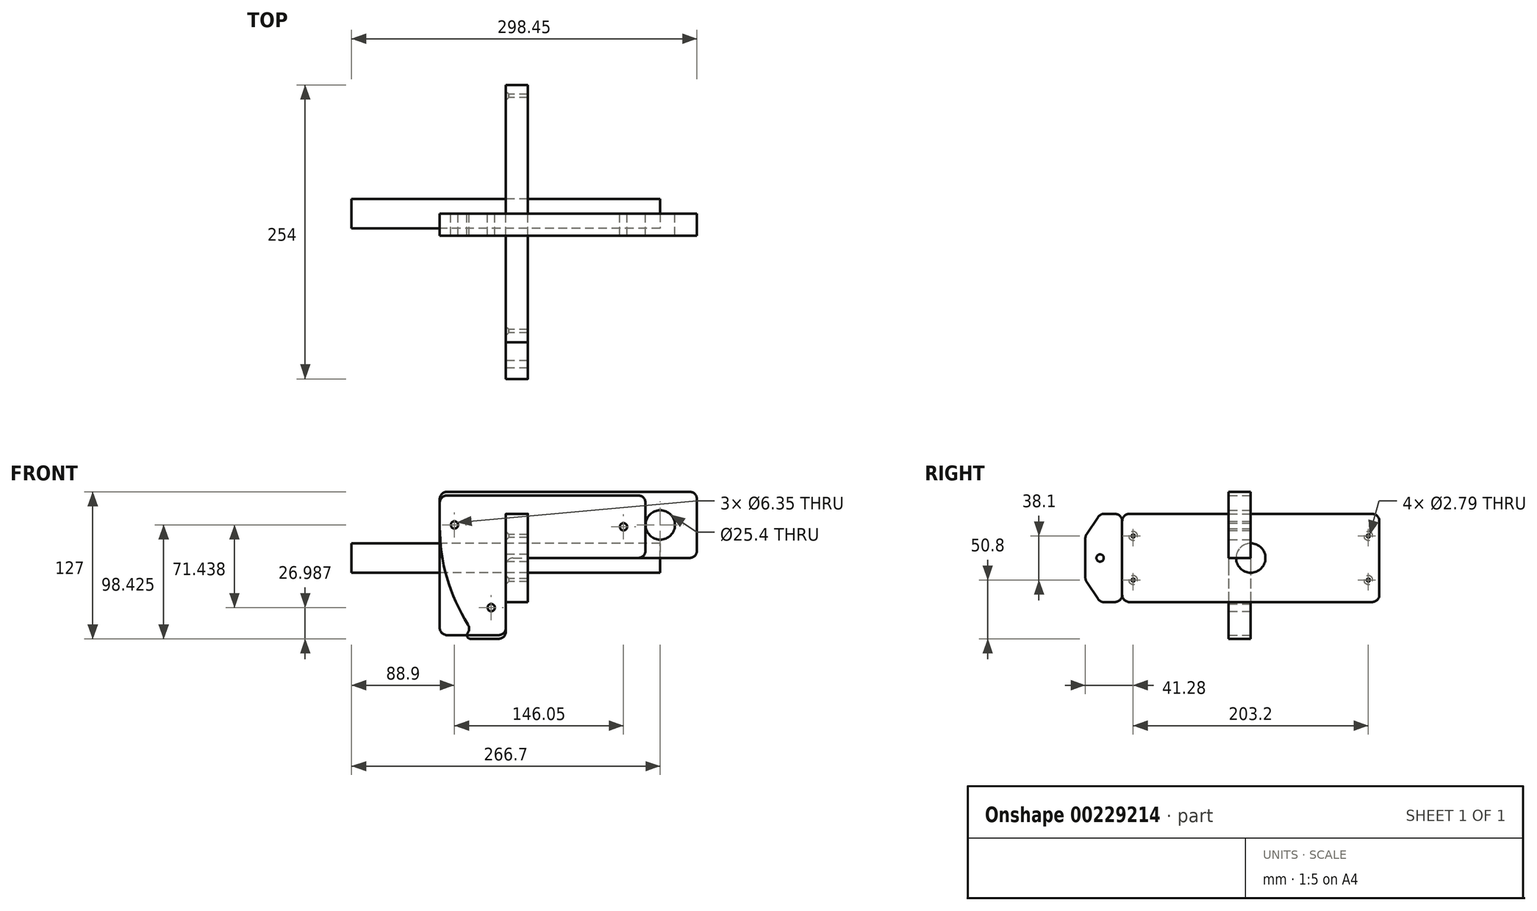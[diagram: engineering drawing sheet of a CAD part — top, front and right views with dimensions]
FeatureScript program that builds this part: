
annotation { "Feature Type Name" : "Feature", "Feature Type Description" : "" }
export const myFeature = defineFeature(function(context is Context, id is Id, definition is map)
    precondition{}
    {
        {
            var Q0;
            Q0=qCreatedBy(makeId("Front.planeOp"),FACE);
            var sketch = newSketch(context, id + "F0", { "sketchPlane" : qUnion([Q0])});
            skLineSegment(sketch, "E0", {"start": v(0, 0) * mm, "end": v(165.1, 0) * mm});
            skLineSegment(sketch, "E1", {"start": v(165.1, 0) * mm, "end": v(165.1, 57.15) * mm});
            skLineSegment(sketch, "E2", {"start": v(165.1, 57.15) * mm, "end": v(-57.15, 57.15) * mm});
            skLineSegment(sketch, "E3", {"start": v(-57.15, 57.15) * mm, "end": v(-57.15, -66.68) * mm});
            skLineSegment(sketch, "E4", {"start": v(-57.15, -66.68) * mm, "end": v(0, -66.68) * mm});
            skLineSegment(sketch, "E5", {"start": v(0, -66.68) * mm, "end": v(0, 0) * mm});
            skCircle(sketch, "E6", {"center": v(133.35, 28.58) * mm, "radius": 12.7 * mm});
            skPoint(sketch, "E6.centerSnap0", {"position": v(165.1, 28.58) * mm});
            skCircle(sketch, "E7", {"center": v(-44.45, 28.58) * mm, "radius": 3.17 * mm});
            skCircle(sketch, "E8", {"center": v(-12.7, -42.86) * mm, "radius": 3.18 * mm});
            skSolve(sketch);
        }
        {
            var Q0;
            Q0=makeQuery(id+"F0.imprint","IMPRINT",FACE,{"disambiguationData":[TD([[makeQuery(id+"F0.imprint","IMPRINT",EDGE,{"derivedFrom":sQuery(id+"F0.wireOp",EDGE,"E0")}),1.0]])]});
            extrude(context, id + "F1", {"entities" : qUnion([Q0]), "depth" : 19.05 * mm});
        }
        {
            var Q0;
            Q0=makeQuery(id+"F1.opExtrude","SWEPT_EDGE",EDGE,{"disambiguationData":[OSD([sQuery(id+"F0.wireOp",EDGE,"E0"),sQuery(id+"F0.wireOp",EDGE,"E5")])]});
            var Q1;
            Q1=makeQuery(id+"F1.opExtrude","SWEPT_EDGE",EDGE,{"disambiguationData":[OSD([sQuery(id+"F0.wireOp",EDGE,"E2"),sQuery(id+"F0.wireOp",EDGE,"E3")])]});
            var Q2;
            Q2=makeQuery(id+"F1.opExtrude","SWEPT_EDGE",EDGE,{"disambiguationData":[OSD([sQuery(id+"F0.wireOp",EDGE,"E1"),sQuery(id+"F0.wireOp",EDGE,"E2")])]});
            var Q3;
            Q3=makeQuery(id+"F1.opExtrude","SWEPT_EDGE",EDGE,{"disambiguationData":[OSD([sQuery(id+"F0.wireOp",EDGE,"E0"),sQuery(id+"F0.wireOp",EDGE,"E1")])]});
            var Q4;
            Q4=makeQuery(id+"F1.opExtrude","SWEPT_EDGE",EDGE,{"disambiguationData":[OSD([sQuery(id+"F0.wireOp",EDGE,"E3"),sQuery(id+"F0.wireOp",EDGE,"E4")])]});
            var Q5;
            Q5=makeQuery(id+"F1.opExtrude","SWEPT_EDGE",EDGE,{"disambiguationData":[OSD([sQuery(id+"F0.wireOp",EDGE,"E4"),sQuery(id+"F0.wireOp",EDGE,"E5")])]});
            fillet(context, id + "F2", {"entities" : qUnion([Q0, Q1, Q2, Q3, Q4, Q5]), "radius" : 6.35 * mm, "tangentPropagation" : true, "allowEdgeOverflow" : false});
        }
        {
            var Q0;
            Q0=qCreatedBy(makeId("Front.planeOp"),FACE);
            var sketch = newSketch(context, id + "F3", { "sketchPlane" : qUnion([Q0])});
            skLineSegment(sketch, "E9", {"start": v(0, 0) * mm, "end": v(120.65, 0) * mm});
            skLineSegment(sketch, "E10", {"start": v(120.65, 0) * mm, "end": v(120.65, 53.98) * mm});
            skLineSegment(sketch, "E11", {"start": v(120.65, 53.98) * mm, "end": v(-57.15, 53.98) * mm});
            skLineSegment(sketch, "E12", {"start": v(-57.15, 53.97) * mm, "end": v(-57.15, 26.99) * mm});
            skLineSegment(sketch, "E13", {"start": v(0, 0) * mm, "end": v(0, -69.85) * mm});
            skLineSegment(sketch, "E14", {"start": v(0, -69.85) * mm, "end": v(-39.88, -69.85) * mm});
            skLineSegment(sketch, "E15", {"start": v(-39.88, -69.85) * mm, "end": v(-29.4, -62.68) * mm});
            skPoint(sketch, "E16", {"position": v(101.6, 26.99) * mm});
            skPoint(sketch, "E16.positionSnap0", {"position": v(120.65, 26.99) * mm});
            skArc(sketch, "E17", {"start": v(-57.15, 26.99) * mm, "mid": v(-50.05, -19.94) * mm, "end": v(-29.4, -62.68) * mm});
            skLineSegment(sketch, "E18", {"start": v(-29.4, -62.68) * mm, "end": v(-88.17, 23.18) * mm, "construction": true});
            skCircle(sketch, "E19", {"center": v(101.6, 26.99) * mm, "radius": 3.18 * mm});
            skSolve(sketch);
        }
        {
            var Q0;
            Q0=makeQuery(id+"F3.imprint","IMPRINT",FACE,{"disambiguationData":[TD([[makeQuery(id+"F3.imprint","IMPRINT",EDGE,{"derivedFrom":sQuery(id+"F3.wireOp",EDGE,"E9")}),1.0]])]});
            extrude(context, id + "F4", {"entities" : qUnion([Q0]), "depth" : 19.05 * mm});
        }
        {
            var Q0;
            Q0=makeQuery(id+"F4.opExtrude","SWEPT_EDGE",EDGE,{"disambiguationData":[OSD([sQuery(id+"F3.wireOp",EDGE,"E11"),sQuery(id+"F3.wireOp",EDGE,"E12")])]});
            var Q1;
            Q1=makeQuery(id+"F4.opExtrude","SWEPT_EDGE",EDGE,{"disambiguationData":[OSD([sQuery(id+"F3.wireOp",EDGE,"E15"),sQuery(id+"F3.wireOp",EDGE,"E17")])]});
            var Q2;
            Q2=makeQuery(id+"F4.opExtrude","SWEPT_EDGE",EDGE,{"disambiguationData":[OSD([sQuery(id+"F3.wireOp",EDGE,"E13"),sQuery(id+"F3.wireOp",EDGE,"E14")])]});
            var Q3;
            Q3=makeQuery(id+"F4.opExtrude","SWEPT_EDGE",EDGE,{"disambiguationData":[OSD([sQuery(id+"F3.wireOp",EDGE,"E9"),sQuery(id+"F3.wireOp",EDGE,"E13")])]});
            var Q4;
            Q4=makeQuery(id+"F4.opExtrude","SWEPT_EDGE",EDGE,{"disambiguationData":[OSD([sQuery(id+"F3.wireOp",EDGE,"E9"),sQuery(id+"F3.wireOp",EDGE,"E10")])]});
            var Q5;
            Q5=makeQuery(id+"F4.opExtrude","SWEPT_EDGE",EDGE,{"disambiguationData":[OSD([sQuery(id+"F3.wireOp",EDGE,"E10"),sQuery(id+"F3.wireOp",EDGE,"E11")])]});
            fillet(context, id + "F5", {"entities" : qUnion([Q0, Q1, Q2, Q3, Q4, Q5]), "radius" : 6.35 * mm, "tangentPropagation" : true, "allowEdgeOverflow" : false});
        }
        {
            var Q0;
            Q0=makeQuery(id+"F4.opExtrude","SWEPT_EDGE",EDGE,{"disambiguationData":[OSD([sQuery(id+"F3.wireOp",EDGE,"E14"),sQuery(id+"F3.wireOp",EDGE,"E15")])]});
            fillet(context, id + "F6", {"entities" : qUnion([Q0]), "radius" : 3.17 * mm, "tangentPropagation" : true, "allowEdgeOverflow" : false});
        }
        {
            var Q0;
            Q0=qCreatedBy(makeId("Right.planeOp"),FACE);
            var sketch = newSketch(context, id + "F7", { "sketchPlane" : qUnion([Q0])});
            skLineSegment(sketch, "E20.bottom", {"start": v(-111.13, 38.1) * mm, "end": v(111.13, 38.1) * mm});
            skLineSegment(sketch, "E20.top", {"start": v(-111.13, -38.1) * mm, "end": v(111.13, -38.1) * mm});
            skLineSegment(sketch, "E20.left", {"start": v(-111.13, 38.1) * mm, "end": v(-111.13, -38.1) * mm});
            skLineSegment(sketch, "E20.right", {"start": v(111.13, 38.1) * mm, "end": v(111.13, -38.1) * mm});
            skPoint(sketch, "E20.middle", {"position": v(0, 0) * mm});
            skLineSegment(sketch, "E21", {"start": v(-111.13, 38.1) * mm, "end": v(-130.18, 38.1) * mm});
            skLineSegment(sketch, "E22", {"start": v(-130.18, 38.1) * mm, "end": v(-142.88, 19.05) * mm});
            skLineSegment(sketch, "E23", {"start": v(-142.88, 19.05) * mm, "end": v(-142.88, -19.05) * mm});
            skLineSegment(sketch, "E24", {"start": v(-142.88, -19.05) * mm, "end": v(-130.18, -38.1) * mm});
            skLineSegment(sketch, "E25", {"start": v(-130.18, -38.1) * mm, "end": v(-111.13, -38.1) * mm});
            skCircle(sketch, "E26", {"center": v(-130.18, 0) * mm, "radius": 3.18 * mm});
            skPoint(sketch, "E26.centerSnap0", {"position": v(-142.88, 0) * mm});
            skPoint(sketch, "E27", {"position": v(-101.6, 19.05) * mm});
            skPoint(sketch, "E28", {"position": v(-101.6, -19.05) * mm});
            skPoint(sketch, "E29", {"position": v(101.6, -19.05) * mm});
            skPoint(sketch, "E30", {"position": v(101.6, 19.05) * mm});
            skSolve(sketch);
        }
        {
            var Q0;
            Q0=makeQuery(id+"F7.imprint","IMPRINT",FACE,{"disambiguationData":[TD([[makeQuery(id+"F7.imprint","IMPRINT",EDGE,{"derivedFrom":sQuery(id+"F7.wireOp",EDGE,"E20.bottom")}),-1.0]])]});
            extrude(context, id + "F8", {"entities" : qUnion([Q0]), "depth" : 19.05 * mm});
        }
        {
            var Q0;
            Q0=makeQuery(id+"F7.imprint","IMPRINT",FACE,{"disambiguationData":[TD([[makeQuery(id+"F7.imprint","IMPRINT",EDGE,{"derivedFrom":sQuery(id+"F7.wireOp",EDGE,"E20.left")}),-1.0]])]});
            extrude(context, id + "F9", {"entities" : qUnion([Q0]), "depth" : 19.05 * mm});
        }
        {
            var Q0;
            Q0=qCreatedBy(makeId("Right.planeOp"),FACE);
            var sketch = newSketch(context, id + "F10", { "sketchPlane" : qUnion([Q0])});
            skCircle(sketch, "E31", {"center": v(0, 0) * mm, "radius": 12.7 * mm});
            skSolve(sketch);
        }
        {
            var Q0;
            Q0=makeQuery(id+"F10.imprint","IMPRINT",FACE,{"disambiguationData":[TD([[makeQuery(id+"F10.imprint","IMPRINT",EDGE,{"derivedFrom":sQuery(id+"F10.wireOp",EDGE,"E31")}),1.0]])]});
            extrude(context, id + "F11", {"entities" : qUnion([Q0]), "endBound" : BoundingType.SYMMETRIC, "depth" : 266.7 * mm});
        }
        {
            var Q0;
            Q0=makeQuery(id+"F9.opExtrude","SWEPT_EDGE",EDGE,{"disambiguationData":[OSD([sQuery(id+"F7.wireOp",EDGE,"E20.bottom"),sQuery(id+"F7.wireOp",EDGE,"E20.left"),sQuery(id+"F7.wireOp",EDGE,"E21")])]});
            var Q1;
            Q1=makeQuery(id+"F9.opExtrude","SWEPT_EDGE",EDGE,{"disambiguationData":[OSD([sQuery(id+"F7.wireOp",EDGE,"E21"),sQuery(id+"F7.wireOp",EDGE,"E22")])]});
            var Q2;
            Q2=makeQuery(id+"F9.opExtrude","SWEPT_EDGE",EDGE,{"disambiguationData":[OSD([sQuery(id+"F7.wireOp",EDGE,"E22"),sQuery(id+"F7.wireOp",EDGE,"E23")])]});
            var Q3;
            Q3=makeQuery(id+"F9.opExtrude","SWEPT_EDGE",EDGE,{"disambiguationData":[OSD([sQuery(id+"F7.wireOp",EDGE,"E23"),sQuery(id+"F7.wireOp",EDGE,"E24")])]});
            var Q4;
            Q4=makeQuery(id+"F9.opExtrude","SWEPT_EDGE",EDGE,{"disambiguationData":[OSD([sQuery(id+"F7.wireOp",EDGE,"E24"),sQuery(id+"F7.wireOp",EDGE,"E25")])]});
            var Q5;
            Q5=makeQuery(id+"F9.opExtrude","SWEPT_EDGE",EDGE,{"disambiguationData":[OSD([sQuery(id+"F7.wireOp",EDGE,"E20.top"),sQuery(id+"F7.wireOp",EDGE,"E20.left"),sQuery(id+"F7.wireOp",EDGE,"E25")])]});
            var Q6;
            Q6=makeQuery(id+"F8.opExtrude","SWEPT_EDGE",EDGE,{"disambiguationData":[OSD([sQuery(id+"F7.wireOp",EDGE,"E20.bottom"),sQuery(id+"F7.wireOp",EDGE,"E20.left"),sQuery(id+"F7.wireOp",EDGE,"E21")])]});
            var Q7;
            Q7=makeQuery(id+"F8.opExtrude","SWEPT_EDGE",EDGE,{"disambiguationData":[OSD([sQuery(id+"F7.wireOp",EDGE,"E20.top"),sQuery(id+"F7.wireOp",EDGE,"E20.left"),sQuery(id+"F7.wireOp",EDGE,"E25")])]});
            var Q8;
            Q8=makeQuery(id+"F8.opExtrude","SWEPT_EDGE",EDGE,{"disambiguationData":[OSD([sQuery(id+"F7.wireOp",EDGE,"E20.top"),sQuery(id+"F7.wireOp",EDGE,"E20.right")])]});
            var Q9;
            Q9=makeQuery(id+"F8.opExtrude","SWEPT_EDGE",EDGE,{"disambiguationData":[OSD([sQuery(id+"F7.wireOp",EDGE,"E20.bottom"),sQuery(id+"F7.wireOp",EDGE,"E20.right")])]});
            fillet(context, id + "F12", {"entities" : qUnion([Q0, Q1, Q2, Q3, Q4, Q5, Q6, Q7, Q8, Q9]), "radius" : 6.35 * mm, "tangentPropagation" : true, "allowEdgeOverflow" : false});
        }
        {
            var Q0;
            Q0=sQuery(id+"F7.wireOp",VERTEX,"E27");
            var Q1;
            Q1=sQuery(id+"F7.wireOp",VERTEX,"E28");
            var Q2;
            Q2=sQuery(id+"F7.wireOp",VERTEX,"E29");
            var Q3;
            Q3=sQuery(id+"F7.wireOp",VERTEX,"E30");
            var Q4;
            Q4=makeQuery(id+"F8.opExtrude","SWEPT_BODY",BODY,{"disambiguationData":[OSD([sQuery(id+"F7.wireOp",EDGE,"E20.bottom"),sQuery(id+"F7.wireOp",EDGE,"E20.top"),sQuery(id+"F7.wireOp",EDGE,"E20.left"),sQuery(id+"F7.wireOp",EDGE,"E20.right")])]});
            hole(context, id + "F13", {"style" : HoleStyle.C_SINK, "endStyle" : HoleEndStyle.THROUGH, "oppositeDirection" : true, "holeDiameter" : 2.8 * mm, "cSinkDiameter" : 7.62 * mm, "cSinkAngle" : 90 * degree, "locations" : qUnion([Q0, Q1, Q2, Q3]), "scope" : qUnion([Q4]), "isTappedThrough" : true});
        }
    });
